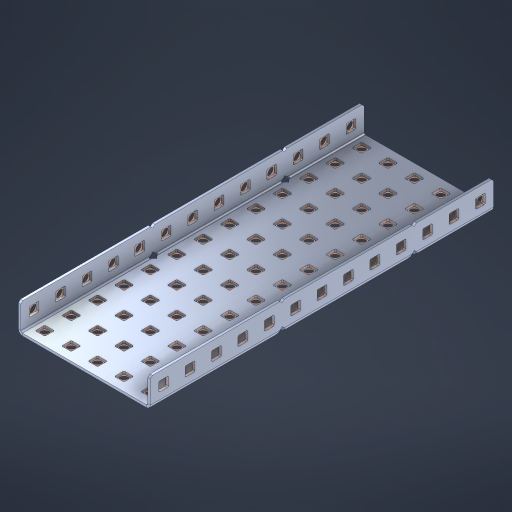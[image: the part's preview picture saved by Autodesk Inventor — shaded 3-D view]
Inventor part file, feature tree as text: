
AUTODESK INVENTOR PART (.ipt)
format: ipt  version: 2023 (Build 270158000, 158)  size: 1,240,576 bytes
history: native  units: in
note: dims shown in document units (in); Inventor stores cm internally (conversion verified against a paired STEP export)
features: other x132, extrude x90, sheet_metal_op x10, sketch x8, mirror x1, pattern_linear x1, chamfer x1
ambient origin geometry x8: Origin, YZ Plane, XZ Plane, XY Plane, X Axis, Y Axis, Z Axis, Center Point
bodies: Solid1 (feature_tree), Body (feature_tree)
feature tree (243):
  other  "Table"
  other  "Steel C 1x5x1x35"
  other  "Steel C 1x5x1x34"
  other  "Steel C 1x5x1x33"
  other  "Steel C 1x5x1x32"
  other  "Steel C 1x5x1x31"
  other  "Steel C 1x5x1x30"
  other  "Steel C 1x5x1x29"
  other  "Steel C 1x5x1x28"
  other  "Steel C 1x5x1x27"
  other  "Steel C 1x5x1x26"
  other  "Steel C 1x5x1x25"
  other  "Steel C 1x5x1x24"
  other  "Steel C 1x5x1x23"
  other  "Steel C 1x5x1x22"
  other  "Steel C 1x5x1x21"
  other  "Steel C 1x5x1x20"
  other  "Steel C 1x5x1x19"
  other  "Steel C 1x5x1x18"
  other  "Steel C 1x5x1x17"
  other  "Steel C 1x5x1x16"
  other  "Steel C 1x5x1x15"
  other  "Steel C 1x5x1x14"
  other  "Steel C 1x5x1x13"
  other  "Steel C 1x5x1x12"
  other  "Steel C 1x5x1x11"
  other  "Steel C 1x5x1x10"
  other  "Steel C 1x5x1x9"
  other  "Steel C 1x5x1x8"
  other  "Steel C 1x5x1x7"
  other  "Steel C 1x5x1x6"
  other  "Steel C 1x5x1x5"
  other  "Steel C 1x5x1x4"
  other  "Steel C 1x5x1x3"
  other  "Steel C 1x5x1x2"
  other  "Steel C 1x5x1x1"
  other  "Flange Pattern Plane"
  sheet_metal_op  "Flange Pattern"
  sheet_metal_op  "Body Pattern"
  other  "Arc Length"
  mirror  "Notch Mirror"
  pattern_linear  "Notch Pattern"  Spacing1=0.1875in  [1 undecoded]
  chamfer  "End Chamfer"
  extrude  "Half Cut"  Depth=0.0469in
  sketch  "Sketch1"  dims[d0=2.5in]
  other  "Plate1"
  sketch  "Sketch2"  dims[d1=6.5in]
  other  "Plate2"
  sheet_metal_op  "Bend1"
  sheet_metal_op  "Corner1"
  sketch  "Sketch3"  dims[d2=0.0469in]
  other  "Flange Pattern Sketch"
  sketch  "Sketch7"  dims[d3=0.0469in]
  other  "Srf1"
  other  "Srf2"
  sketch  "Sketch8"  dims[d4=0.0234in]
  sketch  "Sketch9"  dims[d5=0.0938in]
  other  "Srf91"
  sheet_metal_op  "Body Pattern Sketch"
  other  "Srf92"
  sketch  "Sketch13"  dims[d6=0.0469in]
  sketch  "Sketch14"  dims[d7=0.5in d8=90.0deg d9=0.0312in d10=0.1875in d11=0.0469in d12=0.0469in d16=0.182in d17=0.02in d18=0.0469in d19=0.0in d20=0.25in d21=0.25in d46=0.172in d47=1.0in d48=0.0in d49=0.182in d50=0.02in d51=0.25in d52=0.25in d53=0.0469in d54=0.0in d55=0.172in d56=1.0in d57=0.0in d60=5.1181in d62=0.5in d63=1.9685in d65=0.5in d85=0.1227in d86=0.1659in d88=0.04in d89=0.0469in d90=0.0in d91=0.04in d92=0.0491in d95=2.5in d96=0.04in d97=0.25in d98=45.0deg d101=0.0in d102=2.497in d131=2.5in d132=5.1181in d134=0.5in d139=0.5in]
  other  "Srf856"
  other  "Srf1310"
  other  "Srf1311"
  other  "Srf1312"
  other  "Srf1376"
  other  "Srf1377"
  other  "Srf1728"
  other  "Srf1755"
  other  "Srf1878"
  other  "Srf1879"
  other  "Srf1880"
  other  "Srf1881"
  other  "Srf1882"
  other  "Srf1883"
  other  "Srf1884"
  other  "Srf1885"
  other  "Srf1886"
  other  "Srf1887"
  other  "Srf1888"
  other  "Srf1889"
  other  "Srf1890"
  other  "Srf1891"
  other  "Srf1892"
  other  "Srf1893"
  other  "Srf1894"
  other  "Srf1895"
  other  "Srf1896"
  other  "Srf1897"
  other  "Srf1942"
  other  "Srf1943"
  other  "Srf1944"
  other  "Srf1945"
  other  "Srf1946"
  other  "Srf1947"
  other  "Srf1948"
  other  "Srf1949"
  other  "Srf1950"
  other  "Srf1951"
  other  "Srf1952"
  other  "Srf1953"
  other  "Srf1954"
  other  "Srf1955"
  other  "Srf1956"
  other  "Srf1957"
  other  "Srf1958"
  other  "Srf1959"
  other  "Srf1960"
  other  "Srf1961"
  other  "Srf1962"
  other  "Srf1963"
  other  "Srf1964"
  other  "Srf1965"
  other  "Srf1966"
  other  "Srf1967"
  other  "Srf1968"
  other  "Srf1969"
  other  "Srf1970"
  other  "Srf2146"
  other  "Srf2147"
  other  "Srf2148"
  other  "Srf2149"
  other  "Srf2150"
  other  "Srf2151"
  other  "Srf2152"
  other  "Srf2153"
  other  "Srf2154"
  other  "Srf2155"
  other  "Srf2156"
  other  "Srf2157"
  other  "Srf2158"
  other  "Srf2159"
  other  "Srf2160"
  other  "Srf2161"
  other  "Srf2162"
  other  "Srf2163"
  other  "Srf2164"
  other  "Srf2165"
  other  "Srf2166"
  other  "Srf2167"
  other  "Srf2168"
  other  "Srf2169"
  other  "Srf2170"
  other  "Srf2171"
  other  "Srf2172"
  other  "Srf2173"
  other  "Srf2174"
  other  "Srf2175"
  sheet_metal_op  "Flange Stamp"
  sheet_metal_op  "Flange Circle"
  sheet_metal_op  "Body Stamp"
  sheet_metal_op  "Body Circle"
  sheet_metal_op  "Notch"
  extrude  "ExtrusionSrf2"  Depth=0.0469in
  extrude  "ExtrusionSrf92"  Depth=2.5in
  extrude  "ExtrusionSrf856"  Depth=0.02in
  extrude  "ExtrusionSrf1310"  Depth=0.0469in
  extrude  "ExtrusionSrf1311"  TaperAngle=0.0deg  [1 undecoded]
  extrude  "ExtrusionSrf1312"  Depth=0.25in
  extrude  "ExtrusionSrf1376"  Depth=0.25in
  extrude  "ExtrusionSrf1377"  Depth=2.5in
  extrude  "ExtrusionSrf1728"  Depth=2.5in TaperAngle=0.0deg
  extrude  "ExtrusionSrf1755"  Depth=2.5in
  extrude  "ExtrusionSrf1878"  Depth=0.02in
  extrude  "ExtrusionSrf1879"  Depth=0.25in
  extrude  "ExtrusionSrf1880"  Depth=0.25in
  extrude  "ExtrusionSrf1881"  Depth=0.0469in
  extrude  "ExtrusionSrf1882"  TaperAngle=0.0deg  [1 undecoded]
  extrude  "ExtrusionSrf1883"  Depth=2.5in
  extrude  "ExtrusionSrf1884"  Depth=2.5in TaperAngle=0.0deg
  extrude  "ExtrusionSrf1885"  Depth=2.5in
  extrude  "ExtrusionSrf1886"  Depth=2.5in
  extrude  "ExtrusionSrf1887"  Depth=2.5in
  extrude  "ExtrusionSrf1888"  Depth=2.5in
  extrude  "ExtrusionSrf1889"  Depth=2.5in
  extrude  "ExtrusionSrf1890"  Depth=0.0469in
  extrude  "ExtrusionSrf1891"  TaperAngle=0.0deg  [1 undecoded]
  extrude  "ExtrusionSrf1892"  Depth=2.5in
  extrude  "ExtrusionSrf1893"  Depth=2.5in
  extrude  "ExtrusionSrf1894"  Depth=2.5in
  extrude  "ExtrusionSrf1895"  Depth=0.25in TaperAngle=45.0deg
  extrude  "ExtrusionSrf1896"  TaperAngle=0.0deg  [1 undecoded]
  extrude  "ExtrusionSrf1897"  Depth=2.5in
  extrude  "ExtrusionSrf1942"  Depth=2.5in
  extrude  "ExtrusionSrf1943"  Depth=2.5in
  extrude  "ExtrusionSrf1944"  Depth=2.5in
  extrude  "ExtrusionSrf1945"  Depth=2.5in
  extrude  "ExtrusionSrf1946"  [1 undecoded]
  extrude  "ExtrusionSrf1947"  [1 undecoded]
  extrude  "ExtrusionSrf1948"  [1 undecoded]
  extrude  "ExtrusionSrf1949"  [1 undecoded]
  extrude  "ExtrusionSrf1950"  [1 undecoded]
  extrude  "ExtrusionSrf1951"  [1 undecoded]
  extrude  "ExtrusionSrf1952"  [1 undecoded]
  extrude  "ExtrusionSrf1953"  [1 undecoded]
  extrude  "ExtrusionSrf1954"  [1 undecoded]
  extrude  "ExtrusionSrf1955"  [1 undecoded]
  extrude  "ExtrusionSrf1956"  [1 undecoded]
  extrude  "ExtrusionSrf1957"  [1 undecoded]
  extrude  "ExtrusionSrf1958"  [1 undecoded]
  extrude  "ExtrusionSrf1959"  [1 undecoded]
  extrude  "ExtrusionSrf1960"  [1 undecoded]
  extrude  "ExtrusionSrf1961"  [1 undecoded]
  extrude  "ExtrusionSrf1962"  [1 undecoded]
  extrude  "ExtrusionSrf1963"  [1 undecoded]
  extrude  "ExtrusionSrf1964"  [1 undecoded]
  extrude  "ExtrusionSrf1965"  [1 undecoded]
  extrude  "ExtrusionSrf1966"  [1 undecoded]
  extrude  "ExtrusionSrf1967"  [1 undecoded]
  extrude  "ExtrusionSrf1968"  [1 undecoded]
  extrude  "ExtrusionSrf1969"  [1 undecoded]
  extrude  "ExtrusionSrf1970"  [1 undecoded]
  extrude  "ExtrusionSrf2146"  [1 undecoded]
  extrude  "ExtrusionSrf2147"  [1 undecoded]
  extrude  "ExtrusionSrf2148"  [1 undecoded]
  extrude  "ExtrusionSrf2149"  [1 undecoded]
  extrude  "ExtrusionSrf2150"  [1 undecoded]
  extrude  "ExtrusionSrf2151"  [1 undecoded]
  extrude  "ExtrusionSrf2152"  [1 undecoded]
  extrude  "ExtrusionSrf2153"  [1 undecoded]
  extrude  "ExtrusionSrf2154"  [1 undecoded]
  extrude  "ExtrusionSrf2155"  [1 undecoded]
  extrude  "ExtrusionSrf2156"  [1 undecoded]
  extrude  "ExtrusionSrf2157"  [1 undecoded]
  extrude  "ExtrusionSrf2158"  [1 undecoded]
  extrude  "ExtrusionSrf2159"  [1 undecoded]
  extrude  "ExtrusionSrf2160"  [1 undecoded]
  extrude  "ExtrusionSrf2161"  [1 undecoded]
  extrude  "ExtrusionSrf2162"  [1 undecoded]
  extrude  "ExtrusionSrf2163"  [1 undecoded]
  extrude  "ExtrusionSrf2164"  [1 undecoded]
  extrude  "ExtrusionSrf2165"  [1 undecoded]
  extrude  "ExtrusionSrf2166"  [1 undecoded]
  extrude  "ExtrusionSrf2167"  [1 undecoded]
  extrude  "ExtrusionSrf2168"  [1 undecoded]
  extrude  "ExtrusionSrf2169"  [1 undecoded]
  extrude  "ExtrusionSrf2170"  [1 undecoded]
  extrude  "ExtrusionSrf2171"  [1 undecoded]
  extrude  "ExtrusionSrf2172"  [1 undecoded]
  extrude  "ExtrusionSrf2173"  [1 undecoded]
  extrude  "ExtrusionSrf2174"  [1 undecoded]
  extrude  "ExtrusionSrf2175"  [1 undecoded]
note: 60 required parameter values undecoded (feature->parameter linkage not recoverable at this tier; creation-order binding heuristic only, values carry confidence <= 0.55)
